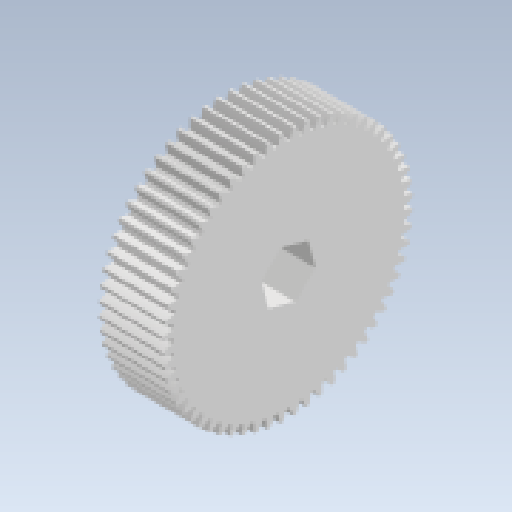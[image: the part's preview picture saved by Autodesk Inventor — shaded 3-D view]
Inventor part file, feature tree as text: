
AUTODESK INVENTOR PART (.ipt)
format: ipt  version: 2023 (Build 270158000, 158)  size: 477,184 bytes
history: native  units: in
note: dims shown in document units (in); Inventor stores cm internally (conversion verified against a paired STEP export)
features: extrude x2, sketch x2, other x1
ambient origin geometry x8: Origin, YZ Plane, XZ Plane, XY Plane, X Axis, Y Axis, Z Axis, Center Point
bodies: Solid1 (feature_tree)
feature tree (5):
  extrude  "Extrusion1"  TaperAngle=0.0deg  [1 undecoded]
  extrude  "Extrusion2"  Depth=0.375in
  sketch  "Sketch1"  dims[d0=0.5in d1=0.0in d2=0.0in]
  sketch  "Sketch2"  dims[d4=0.0in d5=0.0in d6=0.375in]
  other  "TeethCuts"
note: 1 required parameter value undecoded (feature->parameter linkage not recoverable at this tier; creation-order binding heuristic only, values carry confidence <= 0.55)
